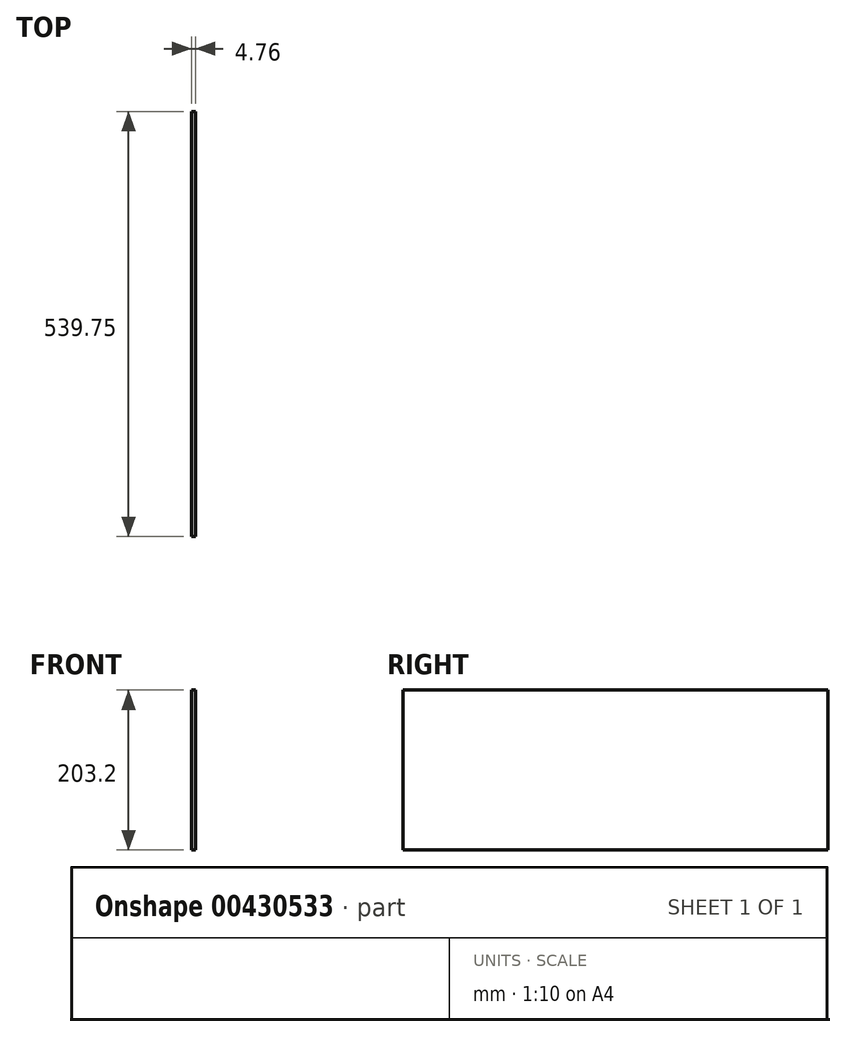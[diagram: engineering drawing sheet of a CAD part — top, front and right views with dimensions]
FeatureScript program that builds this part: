
annotation { "Feature Type Name" : "Feature", "Feature Type Description" : "" }
export const myFeature = defineFeature(function(context is Context, id is Id, definition is map)
    precondition{}
    {
        {
            var Q0;
            Q0=qCreatedBy(makeId("Right.planeOp"),FACE);
            var sketch = newSketch(context, id + "F0", { "sketchPlane" : qUnion([Q0])});
            skLineSegment(sketch, "E0.bottom", {"start": v(-275, -68.21) * mm, "end": v(264.76, -68.21) * mm});
            skLineSegment(sketch, "E0.top", {"start": v(-275, -271.41) * mm, "end": v(264.76, -271.41) * mm});
            skLineSegment(sketch, "E0.left", {"start": v(-275, -68.21) * mm, "end": v(-275, -271.41) * mm});
            skLineSegment(sketch, "E0.right", {"start": v(264.76, -68.21) * mm, "end": v(264.76, -271.41) * mm});
            skSolve(sketch);
        }
        {
            var Q0;
            Q0=makeQuery(id+"F0.imprint","IMPRINT",FACE,{"disambiguationData":[TD([[makeQuery(id+"F0.imprint","IMPRINT",EDGE,{"derivedFrom":sQuery(id+"F0.wireOp",EDGE,"E0.bottom")}),-1.0]])]});
            extrude(context, id + "F1", {"entities" : qUnion([Q0]), "depth" : 4.76 * mm});
        }
    });
